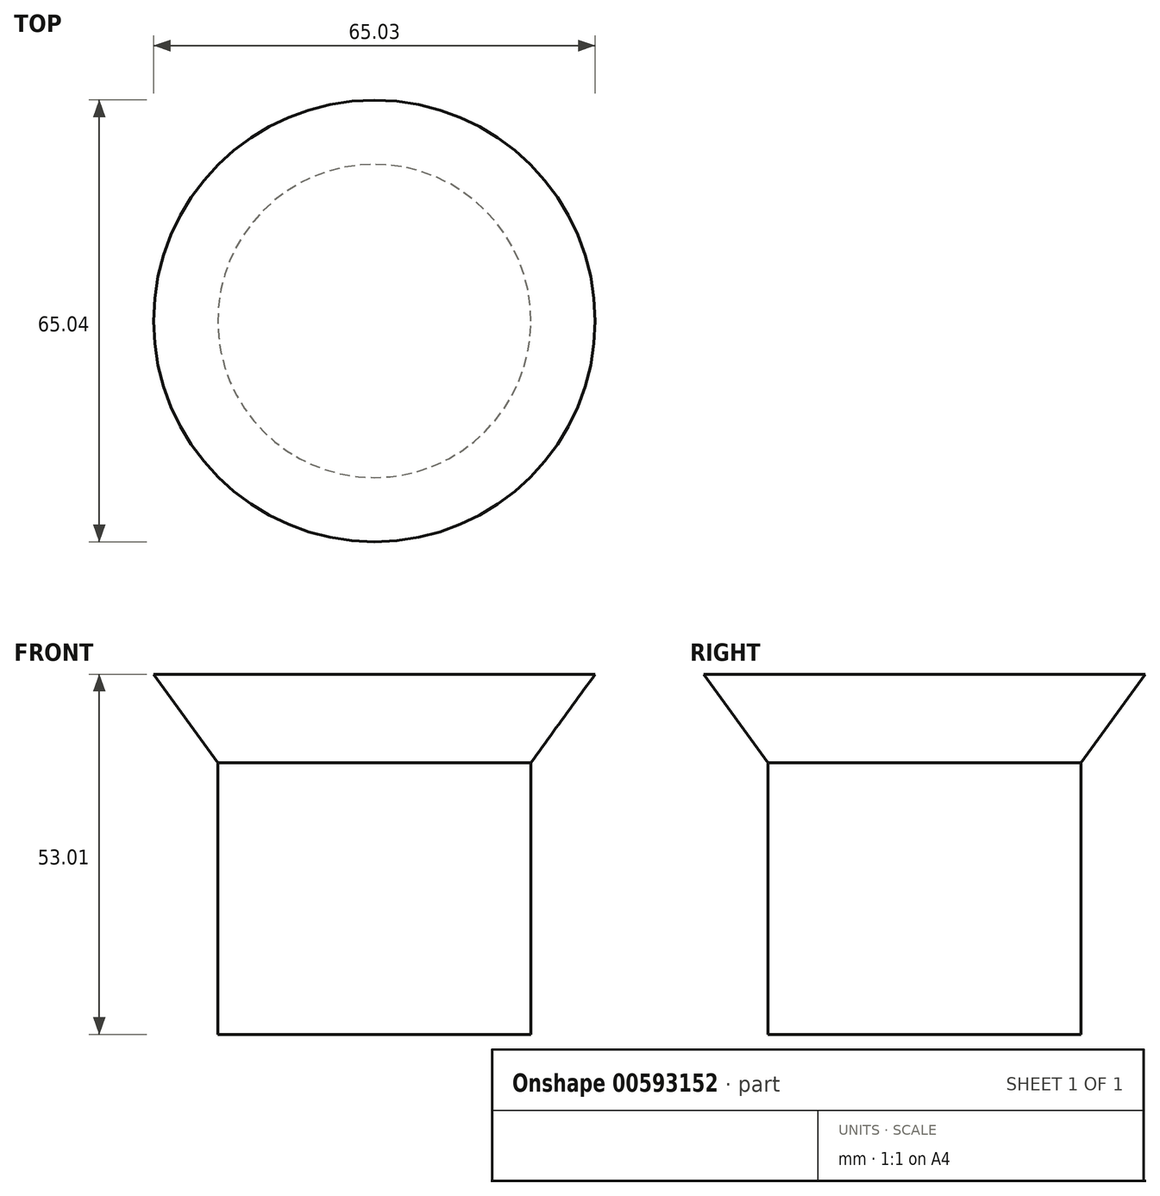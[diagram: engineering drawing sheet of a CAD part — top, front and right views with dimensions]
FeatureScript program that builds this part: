
annotation { "Feature Type Name" : "Feature", "Feature Type Description" : "" }
export const myFeature = defineFeature(function(context is Context, id is Id, definition is map)
    precondition{}
    {
        {
            var Q0;
            Q0=qCreatedBy(makeId("Front.planeOp"),FACE);
            var sketch = newSketch(context, id + "F0", { "sketchPlane" : qUnion([Q0])});
            skLineSegment(sketch, "E0", {"start": v(-11.53, 33.4) * mm, "end": v(20.99, 33.4) * mm});
            skLineSegment(sketch, "E1", {"start": v(20.99, 33.4) * mm, "end": v(11.53, 20.4) * mm});
            skLineSegment(sketch, "E2", {"start": v(11.53, -19.6) * mm, "end": v(11.53, 20.4) * mm});
            skLineSegment(sketch, "E3", {"start": v(11.53, -19.6) * mm, "end": v(-11.53, -19.6) * mm});
            skLineSegment(sketch, "E4", {"start": v(-11.53, 33.4) * mm, "end": v(-11.53, -19.6) * mm});
            skLineSegment(sketch, "E5", {"start": v(-11.53, 33.4) * mm, "end": v(-11.53, 47.8) * mm});
            skSolve(sketch);
        }
        {
            var Q0;
            Q0=makeQuery(id+"F0.imprint","IMPRINT",FACE,{"disambiguationData":[TD([[makeQuery(id+"F0.imprint","IMPRINT",EDGE,{"derivedFrom":sQuery(id+"F0.wireOp",EDGE,"E0")}),-1.0]])]});
            var Q1;
            Q1=sQuery(id+"F0.wireOp",EDGE,"E4");
            revolve(context, id + "F1", {"entities" : qUnion([Q0]), "axis" : qUnion([Q1]), "revolveType" : RevolveType.FULL});
        }
    });
